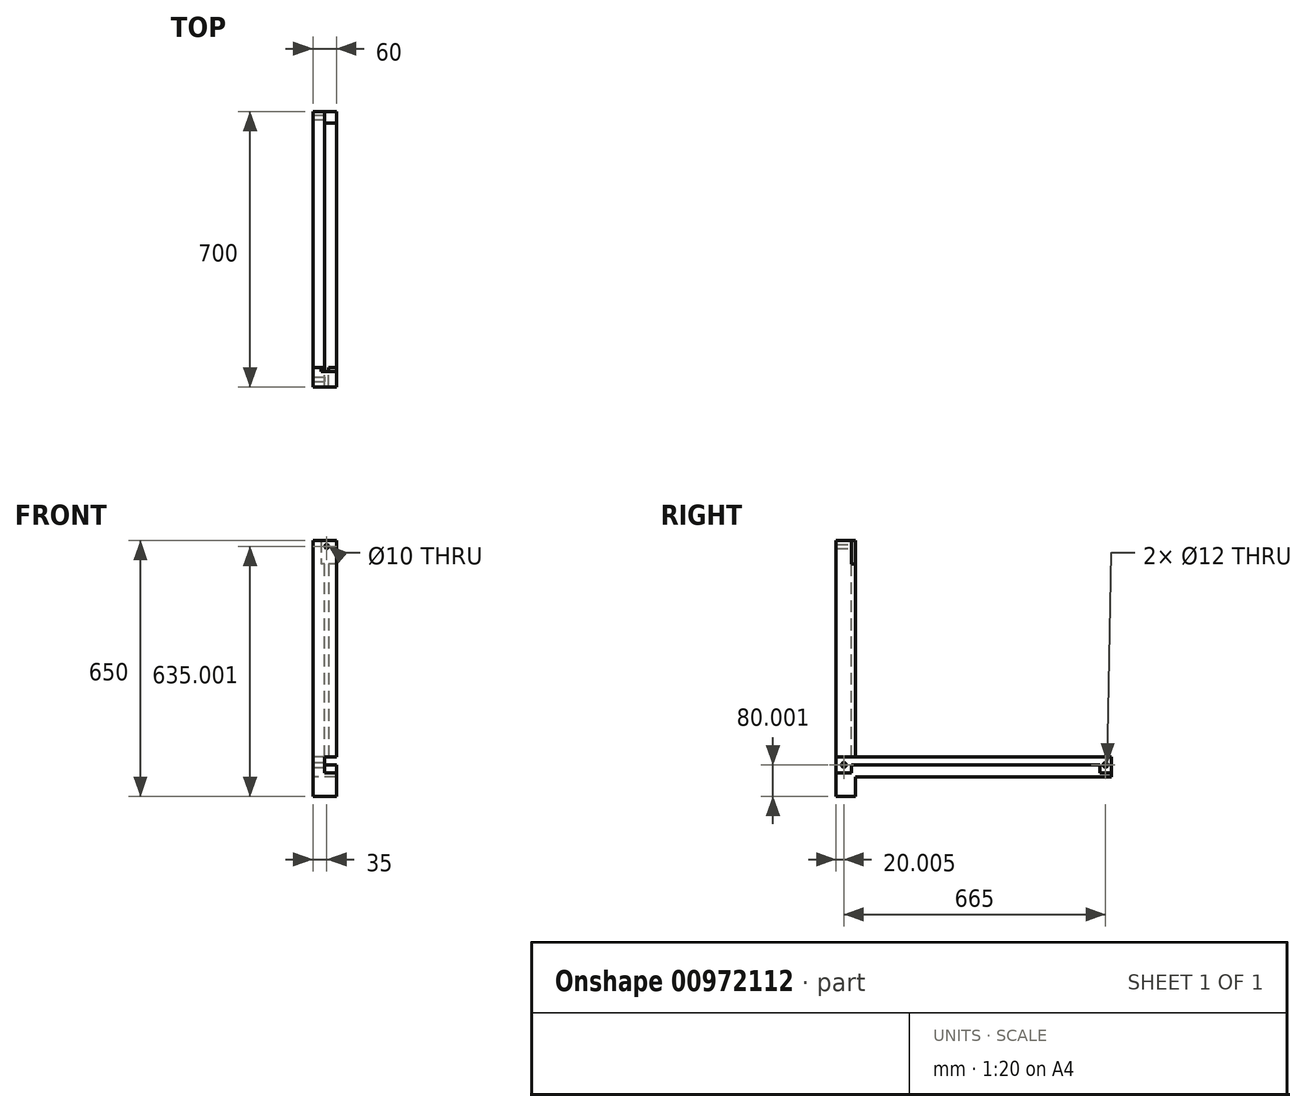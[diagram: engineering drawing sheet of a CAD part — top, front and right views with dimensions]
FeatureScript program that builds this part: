
annotation { "Feature Type Name" : "Feature", "Feature Type Description" : "" }
export const myFeature = defineFeature(function(context is Context, id is Id, definition is map)
    precondition{}
    {
        {
            var Q0;
            Q0=qCreatedBy(makeId("Right.planeOp"),FACE);
            var sketch = newSketch(context, id + "F0", { "sketchPlane" : qUnion([Q0])});
            skLineSegment(sketch, "E0.bottom", {"start": v(-299.4, -86.85) * mm, "end": v(350.6, -86.85) * mm});
            skLineSegment(sketch, "E0.top", {"start": v(-299.4, -36.85) * mm, "end": v(350.6, -36.85) * mm});
            skLineSegment(sketch, "E0.left", {"start": v(-349.4, -86.85) * mm, "end": v(-349.4, -36.85) * mm});
            skLineSegment(sketch, "E0.right", {"start": v(350.6, -86.85) * mm, "end": v(350.6, -36.85) * mm});
            skLineSegment(sketch, "E1", {"start": v(0.6, 119.74) * mm, "end": v(0.6, -301.99) * mm, "construction": true});
            skLineSegment(sketch, "E2.top", {"start": v(-349.4, 513.15) * mm, "end": v(-299.4, 513.15) * mm});
            skLineSegment(sketch, "E2.left", {"start": v(-349.4, -36.85) * mm, "end": v(-349.4, 513.15) * mm});
            skLineSegment(sketch, "E2.right", {"start": v(-299.4, -36.85) * mm, "end": v(-299.4, 513.15) * mm});
            skLineSegment(sketch, "E3.top", {"start": v(-349.4, -136.85) * mm, "end": v(-299.4, -136.85) * mm});
            skLineSegment(sketch, "E3.left", {"start": v(-349.4, -86.85) * mm, "end": v(-349.4, -136.85) * mm});
            skLineSegment(sketch, "E3.right", {"start": v(-299.4, -86.85) * mm, "end": v(-299.4, -136.85) * mm});
            skSolve(sketch);
        }
        {
            var Q0;
            Q0 = qSketchRegion(id + "F0", true);
            extrude(context, id + "F1", {"entities" : qUnion([Q0]), "depth" : 60 * mm, "offsetDistance" : 25 * mm});
        }
        {
            var Q0;
            Q0=makeQuery(id+"F1.opExtrude","CAP_FACE",FACE,{"disambiguationData":[OSD([sQuery(id+"F0.wireOp",EDGE,"E0.bottom"),sQuery(id+"F0.wireOp",EDGE,"E0.top"),sQuery(id+"F0.wireOp",EDGE,"E0.left"),sQuery(id+"F0.wireOp",EDGE,"E0.right"),sQuery(id+"F0.wireOp",EDGE,"E2.top"),sQuery(id+"F0.wireOp",EDGE,"E2.left"),sQuery(id+"F0.wireOp",EDGE,"E2.right"),sQuery(id+"F0.wireOp",EDGE,"E3.top"),sQuery(id+"F0.wireOp",EDGE,"E3.left"),sQuery(id+"F0.wireOp",EDGE,"E3.right")])],"isStart":false});
            var sketch = newSketch(context, id + "F2", { "sketchPlane" : qUnion([Q0])});
            skPoint(sketch, "E4.firstSnap0", {"position": v(-324.4, -136.85) * mm});
            skLineSegment(sketch, "E5.bottom", {"start": v(-349.4, -36.85) * mm, "end": v(-309.4, -36.85) * mm});
            skLineSegment(sketch, "E5.top", {"start": v(-349.4, -76.85) * mm, "end": v(-309.4, -76.85) * mm});
            skLineSegment(sketch, "E5.left", {"start": v(-349.4, -36.85) * mm, "end": v(-349.4, -76.85) * mm});
            skLineSegment(sketch, "E5.right", {"start": v(-309.4, -56.85) * mm, "end": v(-309.4, -76.85) * mm});
            skLineSegment(sketch, "E6", {"start": v(-309.4, -36.85) * mm, "end": v(350.6, -36.85) * mm});
            skLineSegment(sketch, "E7", {"start": v(350.6, -36.85) * mm, "end": v(350.6, -76.85) * mm});
            skLineSegment(sketch, "E8", {"start": v(350.6, -76.85) * mm, "end": v(320.6, -76.85) * mm});
            skLineSegment(sketch, "E9", {"start": v(320.6, -76.85) * mm, "end": v(320.6, -56.85) * mm});
            skLineSegment(sketch, "E10", {"start": v(320.6, -56.85) * mm, "end": v(-309.4, -56.85) * mm});
            skPoint(sketch, "E10.endSnap0", {"position": v(-309.4, -56.85) * mm});
            skSolve(sketch);
        }
        {
            var Q0;
            Q0 = qSketchRegion(id + "F2", true);
            extrude(context, id + "F3", {"entities" : qUnion([Q0]), "operationType" : NewBodyOperationType.REMOVE, "oppositeDirection" : true, "depth" : 30 * mm, "offsetDistance" : 25 * mm});
        }
        {
            var Q0;
            Q0=makeQuery(id+"F3.boolean.opBoolean","COPY",FACE,{"derivedFrom":makeQuery(id+"F3.opExtrude","CAP_FACE",FACE,{"disambiguationData":[OSD([sQuery(id+"F2.wireOp",EDGE,"E5.bottom"),sQuery(id+"F2.wireOp",EDGE,"E5.top"),sQuery(id+"F2.wireOp",EDGE,"E5.left"),sQuery(id+"F2.wireOp",EDGE,"E5.right"),sQuery(id+"F2.wireOp",EDGE,"E6"),sQuery(id+"F2.wireOp",EDGE,"E7"),sQuery(id+"F2.wireOp",EDGE,"E8"),sQuery(id+"F2.wireOp",EDGE,"E9"),sQuery(id+"F2.wireOp",EDGE,"E10")])],"isStart":false})});
            var sketch = newSketch(context, id + "F4", { "sketchPlane" : qUnion([Q0])});
            skPoint(sketch, "E11", {"position": v(-329.4, -56.85) * mm});
            skPoint(sketch, "E12", {"position": v(335.6, -56.85) * mm});
            skPoint(sketch, "E12.positionSnap0", {"position": v(350.6, -56.85) * mm});
            skSolve(sketch);
        }
        {
            var Q0;
            Q0=sQuery(id+"F4.wireOp",VERTEX,"E11");
            var Q1;
            Q1=sQuery(id+"F4.wireOp",VERTEX,"E12");
            var Q2;
            Q2=makeQuery(id+"F1.opExtrude","SWEPT_BODY",BODY,{"disambiguationData":[OSD([sQuery(id+"F0.wireOp",EDGE,"E0.bottom"),sQuery(id+"F0.wireOp",EDGE,"E0.top"),sQuery(id+"F0.wireOp",EDGE,"E0.left"),sQuery(id+"F0.wireOp",EDGE,"E0.right"),sQuery(id+"F0.wireOp",EDGE,"E2.top"),sQuery(id+"F0.wireOp",EDGE,"E2.left"),sQuery(id+"F0.wireOp",EDGE,"E2.right"),sQuery(id+"F0.wireOp",EDGE,"E3.top"),sQuery(id+"F0.wireOp",EDGE,"E3.left"),sQuery(id+"F0.wireOp",EDGE,"E3.right")])]});
            hole(context, id + "F5", {"style" : HoleStyle.SIMPLE, "endStyle" : HoleEndStyle.THROUGH, "holeDiameter" : 12 * mm, "majorDiameter" : 5 * mm, "isTappedThrough" : true, "tappedDepth" : 12 * mm, "tapClearance" : 3, "locations" : qUnion([Q0, Q1]), "scope" : qUnion([Q2])});
        }
        {
            var Q0;
            Q0=makeQuery(id+"F1.opExtrude","SWEPT_FACE",FACE,{"disambiguationData":[OSD([sQuery(id+"F0.wireOp",EDGE,"E2.right")])]});
            var sketch = newSketch(context, id + "F6", { "sketchPlane" : qUnion([Q0])});
            skLineSegment(sketch, "E13", {"start": v(-30, -36.85) * mm, "end": v(-30, 453.15) * mm});
            skLineSegment(sketch, "E14", {"start": v(-40, 453.15) * mm, "end": v(-40, -36.85) * mm});
            skLineSegment(sketch, "E15", {"start": v(-40, -36.85) * mm, "end": v(-30, -36.85) * mm});
            skLineSegment(sketch, "E16", {"start": v(-60, 463.15) * mm, "end": v(-60, 453.15) * mm});
            skLineSegment(sketch, "E17", {"start": v(-60, 453.15) * mm, "end": v(-40, 453.15) * mm});
            skLineSegment(sketch, "E18", {"start": v(-60, 513.15) * mm, "end": v(-60, 463.15) * mm});
            skLineSegment(sketch, "E19", {"start": v(-60, 513.15) * mm, "end": v(-20, 513.15) * mm});
            skLineSegment(sketch, "E20", {"start": v(-20, 513.15) * mm, "end": v(-20, 453.15) * mm});
            skLineSegment(sketch, "E21", {"start": v(-30, 453.15) * mm, "end": v(-20, 453.15) * mm});
            skSolve(sketch);
        }
        {
            var Q0;
            Q0=makeQuery(id+"F6.imprint","IMPRINT",FACE,{"disambiguationData":[TD([[makeQuery(id+"F6.imprint","IMPRINT",EDGE,{"derivedFrom":sQuery(id+"F6.wireOp",EDGE,"E13")}),1.0]])]});
            extrude(context, id + "F7", {"entities" : qUnion([Q0]), "operationType" : NewBodyOperationType.REMOVE, "oppositeDirection" : true, "depth" : 10 * mm, "offsetDistance" : 25 * mm});
        }
        {
            var Q0;
            Q0=makeQuery(id+"F7.boolean.opBoolean","COPY",FACE,{"derivedFrom":makeQuery(id+"F7.opExtrude","CAP_FACE",FACE,{"disambiguationData":[OSD([sQuery(id+"F6.wireOp",EDGE,"E13"),sQuery(id+"F6.wireOp",EDGE,"E14"),sQuery(id+"F6.wireOp",EDGE,"E15"),sQuery(id+"F6.wireOp",EDGE,"E16"),sQuery(id+"F6.wireOp",EDGE,"E17"),sQuery(id+"F6.wireOp",EDGE,"E18"),sQuery(id+"F6.wireOp",EDGE,"E19"),sQuery(id+"F6.wireOp",EDGE,"E20"),sQuery(id+"F6.wireOp",EDGE,"E21")])],"isStart":false})});
            var sketch = newSketch(context, id + "F8", { "sketchPlane" : qUnion([Q0])});
            skPoint(sketch, "E22", {"position": v(-35, 498.15) * mm});
            skPoint(sketch, "E22.positionSnap0", {"position": v(-40, 513.15) * mm});
            skPoint(sketch, "E22.positionSnap1", {"position": v(-60, 498.15) * mm});
            skSolve(sketch);
        }
        {
            var Q0;
            Q0=sQuery(id+"F8.wireOp",VERTEX,"E22");
            var Q1;
            Q1=makeQuery(id+"F1.opExtrude","SWEPT_BODY",BODY,{"disambiguationData":[OSD([sQuery(id+"F0.wireOp",EDGE,"E0.bottom"),sQuery(id+"F0.wireOp",EDGE,"E0.top"),sQuery(id+"F0.wireOp",EDGE,"E0.left"),sQuery(id+"F0.wireOp",EDGE,"E0.right"),sQuery(id+"F0.wireOp",EDGE,"E2.top"),sQuery(id+"F0.wireOp",EDGE,"E2.left"),sQuery(id+"F0.wireOp",EDGE,"E2.right"),sQuery(id+"F0.wireOp",EDGE,"E3.top"),sQuery(id+"F0.wireOp",EDGE,"E3.left"),sQuery(id+"F0.wireOp",EDGE,"E3.right")])]});
            hole(context, id + "F9", {"style" : HoleStyle.SIMPLE, "endStyle" : HoleEndStyle.THROUGH, "holeDiameter" : 10 * mm, "majorDiameter" : 5 * mm, "isTappedThrough" : true, "tappedDepth" : 12 * mm, "tapClearance" : 3, "locations" : qUnion([Q0]), "scope" : qUnion([Q1])});
        }
    });
